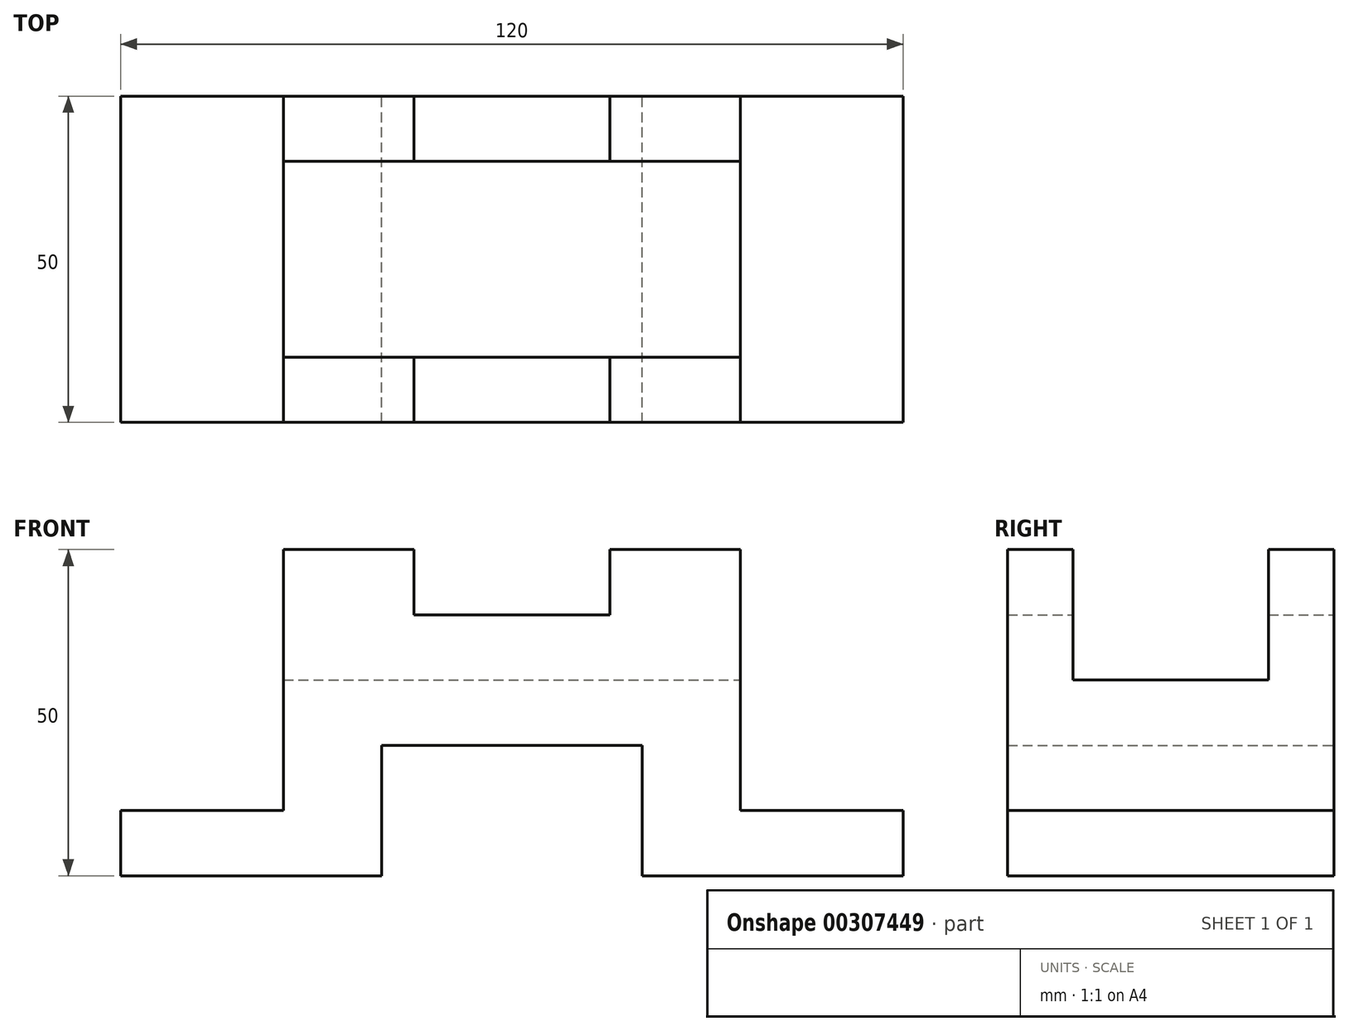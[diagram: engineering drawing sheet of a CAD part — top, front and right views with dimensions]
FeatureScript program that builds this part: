
annotation { "Feature Type Name" : "Feature", "Feature Type Description" : "" }
export const myFeature = defineFeature(function(context is Context, id is Id, definition is map)
    precondition{}
    {
        {
            assignVariable(context, id + "F0", {"name" : "A", "anyValue" : 50});
        }
        {
            var Q0;
            Q0=qCreatedBy(makeId("Front.planeOp"),FACE);
            var sketch = newSketch(context, id + "F1", { "sketchPlane" : qUnion([Q0])});
            skLineSegment(sketch, "E0", {"start": v(0, 0) * mm, "end": v(-20, 0) * mm, "construction": true});
            skLineSegment(sketch, "E1", {"start": v(0, 0) * mm, "end": v(20, 0) * mm, "construction": true});
            skLineSegment(sketch, "E2", {"start": v(-20, 0) * mm, "end": v(-60, 0) * mm});
            skLineSegment(sketch, "E3", {"start": v(20, 0) * mm, "end": v(60, 0) * mm});
            skLineSegment(sketch, "E4", {"start": v(-60, 0) * mm, "end": v(-60, 10) * mm});
            skLineSegment(sketch, "E5", {"start": v(60, 0) * mm, "end": v(60, 10) * mm});
            skLineSegment(sketch, "E6", {"start": v(-60, 10) * mm, "end": v(-35, 10) * mm});
            skLineSegment(sketch, "E7", {"start": v(-35, 10) * mm, "end": v(-35, 50) * mm});
            skLineSegment(sketch, "E8", {"start": v(-35, 50) * mm, "end": v(-15, 50) * mm});
            skLineSegment(sketch, "E9", {"start": v(-15, 50) * mm, "end": v(-15, 40) * mm});
            skLineSegment(sketch, "E10", {"start": v(-15, 40) * mm, "end": v(15, 40) * mm});
            skLineSegment(sketch, "E11", {"start": v(15, 40) * mm, "end": v(15, 50) * mm});
            skLineSegment(sketch, "E12", {"start": v(15, 50) * mm, "end": v(35, 50) * mm});
            skLineSegment(sketch, "E13", {"start": v(35, 50) * mm, "end": v(35, 10) * mm});
            skLineSegment(sketch, "E14", {"start": v(35, 10) * mm, "end": v(60, 10) * mm});
            skLineSegment(sketch, "E15", {"start": v(-20, 0) * mm, "end": v(-20, 20) * mm});
            skLineSegment(sketch, "E16", {"start": v(-20, 20) * mm, "end": v(20, 20) * mm});
            skLineSegment(sketch, "E17", {"start": v(20, 20) * mm, "end": v(20, 0) * mm});
            skSolve(sketch);
        }
        {
            var Q0;
            Q0=makeQuery(id+"F1.imprint","IMPRINT",FACE,{"disambiguationData":[TD([[makeQuery(id+"F1.imprint","IMPRINT",EDGE,{"derivedFrom":sQuery(id+"F1.wireOp",EDGE,"E2")}),-1.0]])]});
            extrude(context, id + "F2", {"entities" : qUnion([Q0]), "depth" : (getVariable(context, 'A')) * mm});
        }
        {
            var Q0;
            Q0=makeQuery(id+"F2.opExtrude","SWEPT_FACE",FACE,{"disambiguationData":[OSD([sQuery(id+"F1.wireOp",EDGE,"E8")])]});
            var sketch = newSketch(context, id + "F3", { "sketchPlane" : qUnion([Q0])});
            skLineSegment(sketch, "E18.bottom", {"start": v(-35, -10) * mm, "end": v(35, -10) * mm});
            skLineSegment(sketch, "E18.top", {"start": v(-35, -40) * mm, "end": v(35, -40) * mm});
            skLineSegment(sketch, "E18.left", {"start": v(-35, -10) * mm, "end": v(-35, -40) * mm});
            skLineSegment(sketch, "E18.right", {"start": v(35, -10) * mm, "end": v(35, -40) * mm});
            skSolve(sketch);
        }
        {
            var Q0;
            Q0 = qSketchRegion(id + "F3", true);
            extrude(context, id + "F4", {"entities" : qUnion([Q0]), "operationType" : NewBodyOperationType.REMOVE, "oppositeDirection" : true, "depth" : 20 * mm});
        }
    });
